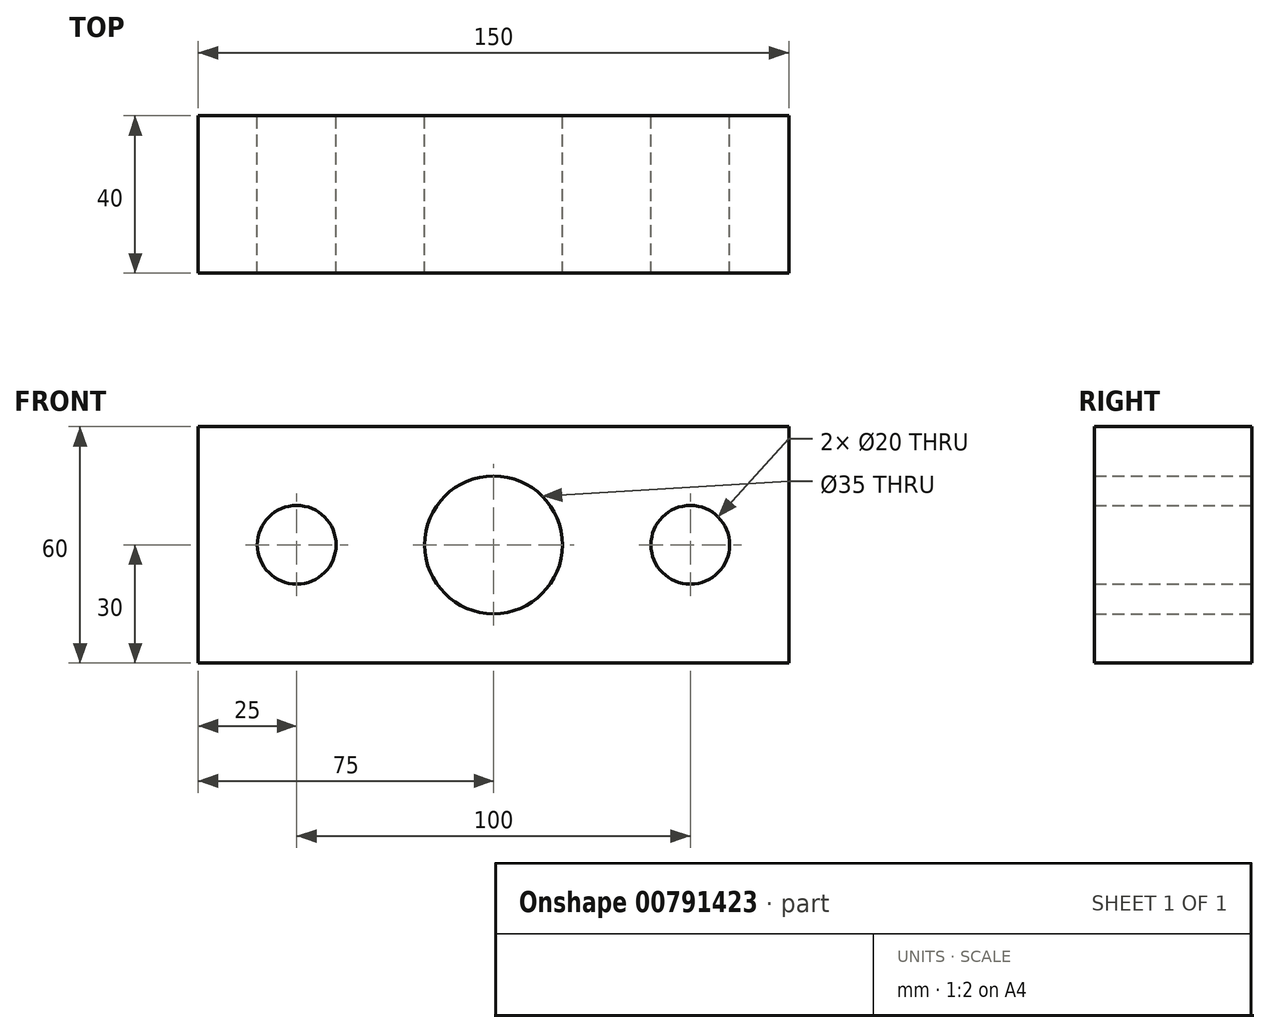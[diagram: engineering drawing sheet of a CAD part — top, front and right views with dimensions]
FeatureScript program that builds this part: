
annotation { "Feature Type Name" : "Feature", "Feature Type Description" : "" }
export const myFeature = defineFeature(function(context is Context, id is Id, definition is map)
    precondition{}
    {
        {
            var Q0;
            Q0=qCreatedBy(makeId("Front.planeOp"),FACE);
            var sketch = newSketch(context, id + "F0", { "sketchPlane" : qUnion([Q0])});
            skLineSegment(sketch, "E0.bottom", {"start": v(-75, 30) * mm, "end": v(75, 30) * mm});
            skLineSegment(sketch, "E0.top", {"start": v(-75, -30) * mm, "end": v(75, -30) * mm});
            skLineSegment(sketch, "E0.left", {"start": v(-75, 30) * mm, "end": v(-75, -30) * mm});
            skLineSegment(sketch, "E0.right", {"start": v(75, 30) * mm, "end": v(75, -30) * mm});
            skCircle(sketch, "E1", {"center": v(0, 0) * mm, "radius": 17.5 * mm});
            skCircle(sketch, "E2", {"center": v(-50, 0) * mm, "radius": 10 * mm});
            skCircle(sketch, "E3", {"center": v(50, 0) * mm, "radius": 10 * mm});
            skSolve(sketch);
        }
        {
            var Q0;
            Q0=makeQuery(id+"F0.imprint","IMPRINT",FACE,{"disambiguationData":[TD([[makeQuery(id+"F0.imprint","IMPRINT",EDGE,{"derivedFrom":sQuery(id+"F0.wireOp",EDGE,"E0.bottom")}),-1.0]])]});
            extrude(context, id + "F1", {"entities" : qUnion([Q0]), "depth" : 40 * mm, "offsetDistance" : 25 * mm});
        }
    });
